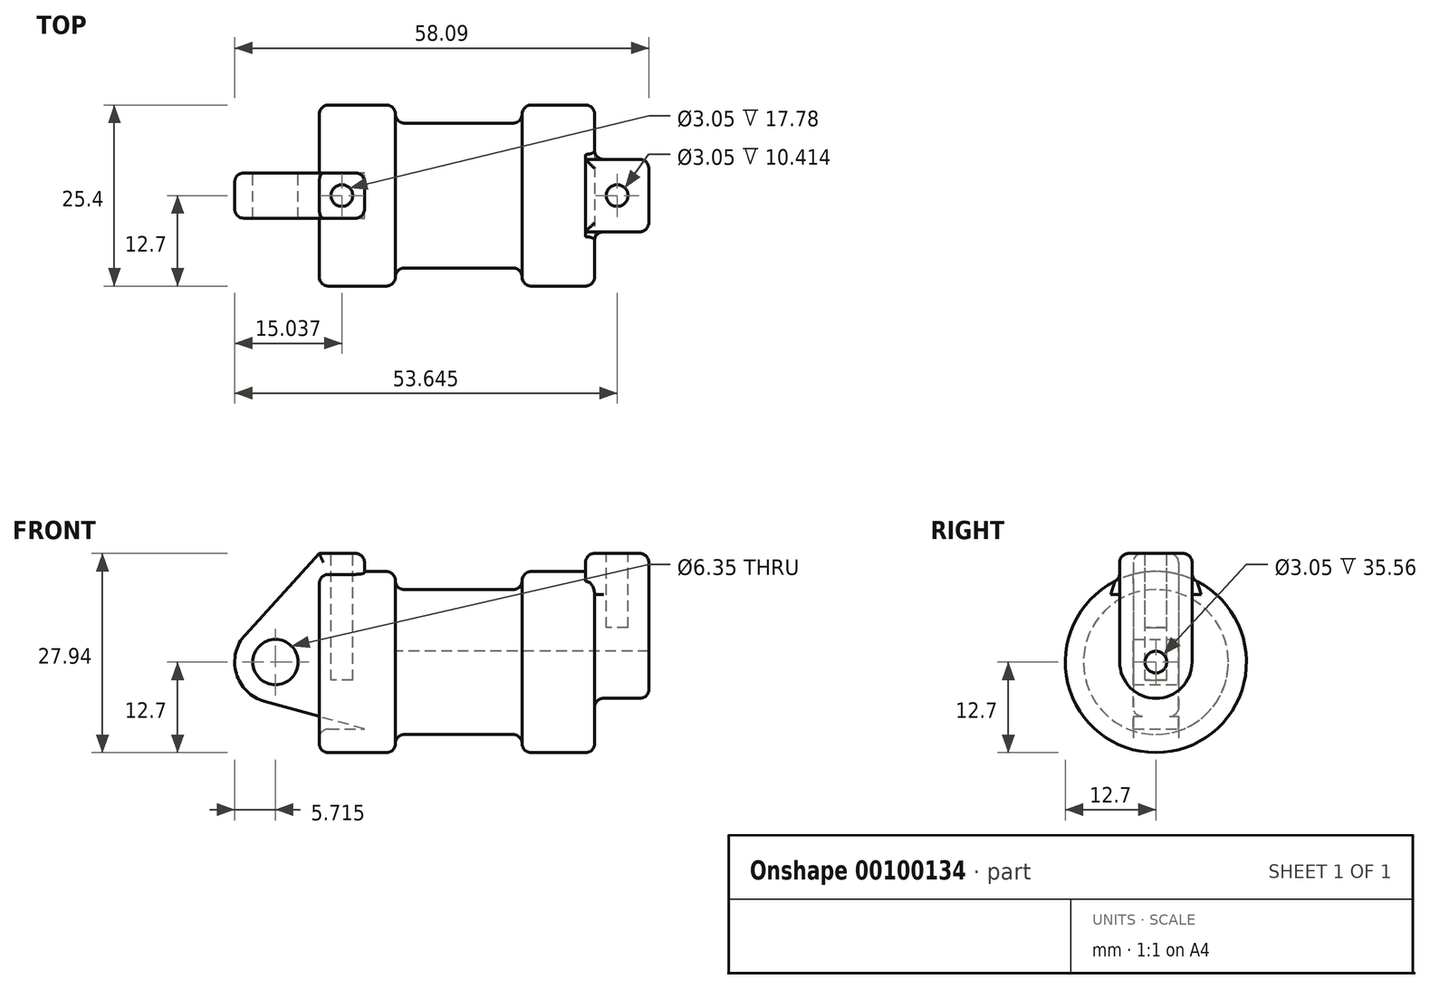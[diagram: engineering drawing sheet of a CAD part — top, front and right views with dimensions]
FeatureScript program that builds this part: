
annotation { "Feature Type Name" : "Feature", "Feature Type Description" : "" }
export const myFeature = defineFeature(function(context is Context, id is Id, definition is map)
    precondition{}
    {
        {
            var Q0;
            Q0=qCreatedBy(makeId("Front.planeOp"),FACE);
            var sketch = newSketch(context, id + "F0", { "sketchPlane" : qUnion([Q0])});
            skLineSegment(sketch, "E0", {"start": v(0, 0) * mm, "end": v(0, 12.7) * mm});
            skLineSegment(sketch, "E1", {"start": v(0, 12.7) * mm, "end": v(10.16, 12.7) * mm});
            skLineSegment(sketch, "E2", {"start": v(10.16, 12.7) * mm, "end": v(10.16, 10.16) * mm});
            skLineSegment(sketch, "E3", {"start": v(10.16, 10.16) * mm, "end": v(27.94, 10.16) * mm});
            skLineSegment(sketch, "E4", {"start": v(27.94, 10.16) * mm, "end": v(27.94, 12.7) * mm});
            skLineSegment(sketch, "E5", {"start": v(27.94, 12.7) * mm, "end": v(38.1, 12.7) * mm});
            skLineSegment(sketch, "E6", {"start": v(38.1, 12.7) * mm, "end": v(38.1, 0) * mm});
            skLineSegment(sketch, "E7", {"start": v(38.1, 0) * mm, "end": v(0, 0) * mm});
            skLineSegment(sketch, "E8", {"start": v(5.84, 15.24) * mm, "end": v(-0.5, 15.24) * mm});
            skLineSegment(sketch, "E9", {"start": v(-0.5, 15.24) * mm, "end": v(-10.88, 3.85) * mm});
            skLineSegment(sketch, "E10", {"start": v(0, 0) * mm, "end": v(-6.65, 0) * mm});
            skCircle(sketch, "E11", {"center": v(-6.65, 0) * mm, "radius": 5.72 * mm});
            skCircle(sketch, "E12", {"center": v(-6.65, 0) * mm, "radius": 3.18 * mm});
            skLineSegment(sketch, "E13", {"start": v(5.84, 15.24) * mm, "end": v(5.84, -9.4) * mm});
            skLineSegment(sketch, "E14", {"start": v(5.84, -9.4) * mm, "end": v(-8.18, -5.5) * mm});
            skSolve(sketch);
        }
        {
            var Q0;
            {var subQ0=sQuery(id+"F0.wireOp",EDGE,"E2");Q0=makeQuery(id+"F0.imprint","IMPRINT",FACE,{"disambiguationData":[TD([[makeQuery(id+"F0.imprint","IMPRINT",EDGE,{"derivedFrom":subQ0}),-1.0]])]});}
            var Q1;
            Q1=sQuery(id+"F0.wireOp",EDGE,"E7");
            revolve(context, id + "F1", {"entities" : qUnion([Q0]), "axis" : qUnion([Q1]), "revolveType" : RevolveType.FULL});
        }
        {
            var Q0;
            {var subQ3=sQuery(id+"F0.wireOp",EDGE,"E0");Q0=makeQuery(id+"F0.imprint","IMPRINT",FACE,{"disambiguationData":[TD([[makeQuery(id+"F0.imprint","IMPRINT",EDGE,{"derivedFrom":subQ3}),1.0]])]});}
            var Q1;
            {var subQ0=sQuery(id+"F0.wireOp",EDGE,"E0");Q1=makeQuery(id+"F0.imprint","IMPRINT",FACE,{"disambiguationData":[TD([[makeQuery(id+"F0.imprint","IMPRINT",EDGE,{"derivedFrom":subQ0}),-1.0]])]});}
            var Q2;
            {var subQ0=sQuery(id+"F0.wireOp",EDGE,"E14");Q2=makeQuery(id+"F0.imprint","IMPRINT",FACE,{"disambiguationData":[TD([[makeQuery(id+"F0.imprint","IMPRINT",EDGE,{"derivedFrom":subQ0}),-1.0]])]});}
            var Q3;
            {var subQ4=sQuery(id+"F0.wireOp",EDGE,"E12");Q3=makeQuery(id+"F0.imprint","IMPRINT",FACE,{"disambiguationData":[TD([[makeQuery(id+"F0.imprint","IMPRINT",EDGE,{"derivedFrom":subQ4}),-1.0]])]});}
            extrude(context, id + "F2", {"entities" : qUnion([Q0, Q1, Q2, Q3]), "operationType" : NewBodyOperationType.ADD, "endBound" : BoundingType.SYMMETRIC, "depth" : 6.35 * mm, "hasSecondDirection" : true, "secondDirectionOppositeDirection" : true, "secondDirectionDepth" : 3.17 * mm});
        }
        {
            var Q0;
            Q0=makeQuery(id+"F1.opRevolve","SWEPT_FACE",FACE,{"disambiguationData":[OSD([sQuery(id+"F0.wireOp",EDGE,"E13")])]});
            extrude(context, id + "F3", {"entities" : qUnion([Q0]), "operationType" : NewBodyOperationType.ADD, "depth" : 6.35 * mm});
        }
        {
            var Q0;
            Q0=makeQuery(id+"F1.opRevolve","SWEPT_FACE",FACE,{"disambiguationData":[OSD([sQuery(id+"F0.wireOp",EDGE,"E6")])]});
            var sketch = newSketch(context, id + "F4", { "sketchPlane" : qUnion([Q0])});
            skCircle(sketch, "E15", {"center": v(0, 0) * mm, "radius": 1.52 * mm});
            skCircle(sketch, "E16", {"center": v(0, 0) * mm, "radius": 5.08 * mm});
            skLineSegment(sketch, "E17", {"start": v(-5.08, 15.24) * mm, "end": v(5.08, 15.24) * mm});
            skLineSegment(sketch, "E18", {"start": v(5.08, 15.24) * mm, "end": v(5.08, 0) * mm});
            skLineSegment(sketch, "E19", {"start": v(-5.08, 15.24) * mm, "end": v(-5.08, 0) * mm});
            skSolve(sketch);
        }
        {
            var Q0;
            {var subQ0=sQuery(id+"F4.wireOp",EDGE,"E18");var subQ1=sQuery(id+"F4.wireOp",EDGE,"E16");var subQ2=makeQuery(id+"F4.imprint","INTERSECT",VERTEX,{"derivedFrom":[subQ1,subQ0]});Q0=makeQuery(id+"F4.imprint","IMPRINT",FACE,{"disambiguationData":[TD([[makeQuery(id+"F4.imprint","IMPRINT",EDGE,{"disambiguationData":[TD([[subQ2,-1.0]])],"derivedFrom":subQ1}),-1.0]])]});}
            var Q1;
            {var subQ0=sQuery(id+"F4.wireOp",EDGE,"E17");Q1=makeQuery(id+"F4.imprint","IMPRINT",FACE,{"disambiguationData":[TD([[makeQuery(id+"F4.imprint","IMPRINT",EDGE,{"derivedFrom":subQ0}),-1.0]])]});}
            var Q2;
            Q2=makeQuery(id+"F4.imprint","IMPRINT",FACE,{"disambiguationData":[TD([[makeQuery(id+"F4.imprint","IMPRINT",EDGE,{"derivedFrom":sQuery(id+"F4.wireOp",EDGE,"E15")}),-1.0]])]});
            extrude(context, id + "F5", {"entities" : qUnion([Q0, Q1, Q2]), "operationType" : NewBodyOperationType.ADD, "depth" : 7.62 * mm, "hasSecondDirection" : true, "secondDirectionOppositeDirection" : true, "secondDirectionDepth" : 1.27 * mm});
        }
        {
            var Q0;
            Q0=makeQuery(id+"F5.boolean.opBoolean","SPLIT",FACE,{"disambiguationData":[TD([makeQuery(id+"F5.opExtrude","SWEPT_FACE",FACE,{"disambiguationData":[OSD([sQuery(id+"F4.wireOp",EDGE,"E15")])]})])],"derivedFrom":makeQuery(id+"F1.opRevolve","SWEPT_FACE",FACE,{"disambiguationData":[OSD([sQuery(id+"F0.wireOp",EDGE,"E6")])]})});
            var Q1;
            Q1=makeQuery(id+"F1.opRevolve","SWEPT_FACE",FACE,{"disambiguationData":[OSD([sQuery(id+"F0.wireOp",EDGE,"E2")])]});
            var Q2;
            Q2=makeQuery(id+"F1.opRevolve","SWEPT_BODY",BODY,{"disambiguationData":[OSD([sQuery(id+"F0.wireOp",EDGE,"E1"),sQuery(id+"F0.wireOp",EDGE,"E2"),sQuery(id+"F0.wireOp",EDGE,"E3"),sQuery(id+"F0.wireOp",EDGE,"E4"),sQuery(id+"F0.wireOp",EDGE,"E5"),sQuery(id+"F0.wireOp",EDGE,"E6"),sQuery(id+"F0.wireOp",EDGE,"E7"),sQuery(id+"F0.wireOp",EDGE,"E13")])]});
            extrude(context, id + "F6", {"entities" : qUnion([Q0]), "operationType" : NewBodyOperationType.ADD, "endBound" : BoundingType.UP_TO_SURFACE, "oppositeDirection" : true, "endBoundEntityFace" : qUnion([Q1]), "endBoundEntityBody" : qUnion([Q2]), "depth" : 25.4 * mm});
        }
        {
            var Q0;
            Q0=makeQuery(id+"F5.boolean.opBoolean","SPLIT",FACE,{"disambiguationData":[TD([makeQuery(id+"F5.opExtrude","SWEPT_FACE",FACE,{"disambiguationData":[OSD([sQuery(id+"F4.wireOp",EDGE,"E15")])]})])],"derivedFrom":makeQuery(id+"F1.opRevolve","SWEPT_FACE",FACE,{"disambiguationData":[OSD([sQuery(id+"F0.wireOp",EDGE,"E6")])]})});
            var Q1;
            Q1=makeQuery(id+"F1.opRevolve","SWEPT_FACE",FACE,{"disambiguationData":[OSD([sQuery(id+"F0.wireOp",EDGE,"E2")])]});
            extrude(context, id + "F7", {"entities" : qUnion([Q0]), "operationType" : NewBodyOperationType.REMOVE, "endBound" : BoundingType.UP_TO_SURFACE, "oppositeDirection" : true, "endBoundEntityFace" : qUnion([Q1]), "depth" : 25.4 * mm});
        }
        {
            var Q0;
            Q0=makeQuery(id+"F2.opExtrude","SWEPT_FACE",FACE,{"disambiguationData":[OSD([sQuery(id+"F0.wireOp",EDGE,"E8")])]});
            var sketch = newSketch(context, id + "F8", { "sketchPlane" : qUnion([Q0])});
            skCircle(sketch, "E20", {"center": v(2.67, 0) * mm, "radius": 1.52 * mm});
            skSolve(sketch);
        }
        {
            var Q0;
            Q0=makeQuery(id+"F8.imprint","IMPRINT",FACE,{"disambiguationData":[TD([[makeQuery(id+"F8.imprint","IMPRINT",EDGE,{"derivedFrom":sQuery(id+"F8.wireOp",EDGE,"E20")}),1.0]])]});
            extrude(context, id + "F9", {"entities" : qUnion([Q0]), "operationType" : NewBodyOperationType.REMOVE, "oppositeDirection" : true, "depth" : 17.78 * mm});
        }
        {
            var Q0;
            Q0=makeQuery(id+"F5.opExtrude","SWEPT_FACE",FACE,{"disambiguationData":[OSD([sQuery(id+"F4.wireOp",EDGE,"E17")])]});
            var sketch = newSketch(context, id + "F10", { "sketchPlane" : qUnion([Q0])});
            skLineSegment(sketch, "E21", {"start": v(36.83, 0) * mm, "end": v(45.72, 0) * mm, "construction": true});
            skCircle(sketch, "E22", {"center": v(41.28, 0) * mm, "radius": 1.52 * mm});
            skSolve(sketch);
        }
        {
            var Q0;
            Q0=makeQuery(id+"F10.imprint","IMPRINT",FACE,{"disambiguationData":[TD([[makeQuery(id+"F10.imprint","IMPRINT",EDGE,{"derivedFrom":sQuery(id+"F10.wireOp",EDGE,"E22")}),1.0]])]});
            extrude(context, id + "F11", {"entities" : qUnion([Q0]), "operationType" : NewBodyOperationType.REMOVE, "oppositeDirection" : true, "depth" : 10.4 * mm});
        }
        {
            var Q0;
            Q0=makeQuery(id+"F2.opExtrude","CAP_EDGE",EDGE,{"disambiguationData":[OSD([sQuery(id+"F0.wireOp",EDGE,"E8")])],"isStart":false});
            var Q1;
            Q1=makeQuery(id+"F2.opExtrude","SWEPT_EDGE",EDGE,{"disambiguationData":[OSD([sQuery(id+"F0.wireOp",EDGE,"E8"),sQuery(id+"F0.wireOp",EDGE,"E13")])]});
            var Q2;
            Q2=makeQuery(id+"F2.opExtrude","CAP_EDGE",EDGE,{"disambiguationData":[OSD([sQuery(id+"F0.wireOp",EDGE,"E8")])],"isStart":true});
            var Q3;
            {var subQ0=sQuery(id+"F0.wireOp",EDGE,"E1");var subQ1=sQuery(id+"F0.wireOp",EDGE,"E13");Q3=makeQuery(id+"F2.boolean.opBoolean","SPLIT",EDGE,{"disambiguationData":[topologyDisambiguationEdgeConnected([makeQuery(id+"F2.opExtrude","SWEPT_FACE",FACE,{"disambiguationData":[OSD([subQ1])]})])],"derivedFrom":makeQuery(id+"F1.opRevolve","SWEPT_EDGE",EDGE,{"disambiguationData":[OSD([subQ0,subQ1])]})});}
            var Q4;
            {var subQ0=sQuery(id+"F0.wireOp",EDGE,"E13");var subQ1=sQuery(id+"F0.wireOp",EDGE,"E14");var subQ2=sQuery(id+"F0.wireOp",EDGE,"E12");var subQ3=sQuery(id+"F0.wireOp",EDGE,"E11");var subQ4=sQuery(id+"F0.wireOp",EDGE,"E9");var subQ5=sQuery(id+"F0.wireOp",EDGE,"E8");var subQ6=sQuery(id+"F0.wireOp",EDGE,"E1");Q4=makeQuery(id+"F3.opExtrude","SWEPT_EDGE",EDGE,{"disambiguationData":[OSD([subQ6,subQ5,subQ4,subQ3,subQ2,subQ0,subQ1]),TDD([makeQuery(id+"F2.boolean.opBoolean","TWEAK_VERTEX",VERTEX,{"derivedFrom":[makeQuery(id+"F1.opRevolve","SWEPT_FACE",FACE,{"disambiguationData":[OSD([subQ6])]}),makeQuery(id+"F1.opRevolve","SWEPT_FACE",FACE,{"disambiguationData":[OSD([subQ0])]}),makeQuery(id+"F2.opExtrude","CAP_FACE",FACE,{"disambiguationData":[OSD([subQ5,subQ4,subQ3,subQ2,subQ0,subQ1])],"isStart":false}),makeQuery(id+"F2.opExtrude","SWEPT_FACE",FACE,{"disambiguationData":[OSD([subQ0])]})]})])]});}
            var Q5;
            {var subQ0=sQuery(id+"F0.wireOp",EDGE,"E13");var subQ1=sQuery(id+"F0.wireOp",EDGE,"E14");var subQ2=sQuery(id+"F0.wireOp",EDGE,"E12");var subQ3=sQuery(id+"F0.wireOp",EDGE,"E11");var subQ4=sQuery(id+"F0.wireOp",EDGE,"E9");var subQ5=sQuery(id+"F0.wireOp",EDGE,"E8");var subQ6=sQuery(id+"F0.wireOp",EDGE,"E1");Q5=makeQuery(id+"F3.opExtrude","SWEPT_EDGE",EDGE,{"disambiguationData":[OSD([subQ6,subQ5,subQ4,subQ3,subQ2,subQ0,subQ1]),TDD([makeQuery(id+"F2.boolean.opBoolean","TWEAK_VERTEX",VERTEX,{"derivedFrom":[makeQuery(id+"F1.opRevolve","SWEPT_FACE",FACE,{"disambiguationData":[OSD([subQ6])]}),makeQuery(id+"F1.opRevolve","SWEPT_FACE",FACE,{"disambiguationData":[OSD([subQ0])]}),makeQuery(id+"F2.opExtrude","CAP_FACE",FACE,{"disambiguationData":[OSD([subQ5,subQ4,subQ3,subQ2,subQ0,subQ1])],"isStart":true}),makeQuery(id+"F2.opExtrude","SWEPT_FACE",FACE,{"disambiguationData":[OSD([subQ0])]})]})])]});}
            var Q6;
            {var subQ0=sQuery(id+"F0.wireOp",EDGE,"E13");Q6=makeQuery(id+"F2.boolean.opBoolean","SPLIT",EDGE,{"disambiguationData":[topologyDisambiguationEdgeConnected([makeQuery(id+"F2.opExtrude","SWEPT_FACE",FACE,{"disambiguationData":[OSD([subQ0])]})])],"derivedFrom":makeQuery(id+"F2.opExtrude","CAP_EDGE",EDGE,{"disambiguationData":[OSD([subQ0])],"isStart":true})});}
            var Q7;
            {var subQ0=sQuery(id+"F0.wireOp",EDGE,"E13");Q7=makeQuery(id+"F2.boolean.opBoolean","SPLIT",EDGE,{"disambiguationData":[topologyDisambiguationEdgeConnected([makeQuery(id+"F2.opExtrude","SWEPT_FACE",FACE,{"disambiguationData":[OSD([subQ0])]})])],"derivedFrom":makeQuery(id+"F2.opExtrude","CAP_EDGE",EDGE,{"disambiguationData":[OSD([subQ0])],"isStart":false})});}
            var Q8;
            Q8=makeQuery(id+"F2.opExtrude","CAP_EDGE",EDGE,{"disambiguationData":[OSD([sQuery(id+"F0.wireOp",EDGE,"E9")])],"isStart":true});
            var Q9;
            Q9=makeQuery(id+"F2.opExtrude","CAP_EDGE",EDGE,{"disambiguationData":[OSD([sQuery(id+"F0.wireOp",EDGE,"E9")])],"isStart":false});
            var Q10;
            Q10=makeQuery(id+"F1.opRevolve","SWEPT_EDGE",EDGE,{"disambiguationData":[OSD([sQuery(id+"F0.wireOp",EDGE,"E1"),sQuery(id+"F0.wireOp",EDGE,"E2")])]});
            var Q11;
            Q11=makeQuery(id+"F1.opRevolve","SWEPT_EDGE",EDGE,{"disambiguationData":[OSD([sQuery(id+"F0.wireOp",EDGE,"E2"),sQuery(id+"F0.wireOp",EDGE,"E3")])]});
            var Q12;
            Q12=makeQuery(id+"F1.opRevolve","SWEPT_EDGE",EDGE,{"disambiguationData":[OSD([sQuery(id+"F0.wireOp",EDGE,"E4"),sQuery(id+"F0.wireOp",EDGE,"E5")])]});
            var Q13;
            Q13=makeQuery(id+"F1.opRevolve","SWEPT_EDGE",EDGE,{"disambiguationData":[OSD([sQuery(id+"F0.wireOp",EDGE,"E3"),sQuery(id+"F0.wireOp",EDGE,"E4")])]});
            var Q14;
            Q14=makeQuery(id+"F1.opRevolve","SWEPT_EDGE",EDGE,{"disambiguationData":[OSD([sQuery(id+"F0.wireOp",EDGE,"E5"),sQuery(id+"F0.wireOp",EDGE,"E6")])]});
            var Q15;
            Q15=makeQuery(id+"F5.opExtrude","SWEPT_EDGE",EDGE,{"disambiguationData":[OSD([sQuery(id+"F4.wireOp",EDGE,"E17"),sQuery(id+"F4.wireOp",EDGE,"E19")])]});
            var Q16;
            Q16=makeQuery(id+"F5.opExtrude","CAP_EDGE",EDGE,{"disambiguationData":[OSD([sQuery(id+"F4.wireOp",EDGE,"E17")])],"isStart":true});
            var Q17;
            Q17=makeQuery(id+"F5.opExtrude","SWEPT_EDGE",EDGE,{"disambiguationData":[OSD([sQuery(id+"F4.wireOp",EDGE,"E17"),sQuery(id+"F4.wireOp",EDGE,"E18")])]});
            var Q18;
            Q18=makeQuery(id+"F5.opExtrude","CAP_EDGE",EDGE,{"disambiguationData":[OSD([sQuery(id+"F4.wireOp",EDGE,"E17")])],"isStart":false});
            var Q19;
            Q19=makeQuery(id+"F5.opExtrude","CAP_EDGE",EDGE,{"disambiguationData":[OSD([sQuery(id+"F4.wireOp",EDGE,"E19")])],"isStart":false});
            var Q20;
            Q20=makeQuery(id+"F5.boolean.opBoolean","INTERSECT",EDGE,{"derivedFrom":[makeQuery(id+"F1.opRevolve","SWEPT_FACE",FACE,{"disambiguationData":[OSD([sQuery(id+"F0.wireOp",EDGE,"E6")])]}),makeQuery(id+"F5.opExtrude","SWEPT_FACE",FACE,{"disambiguationData":[OSD([sQuery(id+"F4.wireOp",EDGE,"E19")])]})]});
            var Q21;
            Q21=makeQuery(id+"F5.boolean.opBoolean","INTERSECT",EDGE,{"derivedFrom":[makeQuery(id+"F1.opRevolve","SWEPT_FACE",FACE,{"disambiguationData":[OSD([sQuery(id+"F0.wireOp",EDGE,"E6")])]}),makeQuery(id+"F5.opExtrude","SWEPT_FACE",FACE,{"disambiguationData":[OSD([sQuery(id+"F4.wireOp",EDGE,"E16")])]})]});
            fillet(context, id + "F12", {"entities" : qUnion([Q0, Q1, Q2, Q3, Q4, Q5, Q6, Q7, Q8, Q9, Q10, Q11, Q12, Q13, Q14, Q15, Q16, Q17, Q18, Q19, Q20, Q21]), "radius" : 1.27 * mm, "tangentPropagation" : true, "allowEdgeOverflow" : false});
        }
        {
            var Q0;
            Q0=makeQuery(id+"F3.opExtrude","CAP_EDGE",EDGE,{"disambiguationData":[OSD([sQuery(id+"F0.wireOp",EDGE,"E1"),sQuery(id+"F0.wireOp",EDGE,"E13")])],"isStart":false});
            var Q1;
            {var subQ0=sQuery(id+"F0.wireOp",EDGE,"E13");var subQ1=makeQuery(id+"F2.opExtrude","CAP_FACE",FACE,{"disambiguationData":[OSD([sQuery(id+"F0.wireOp",EDGE,"E8"),sQuery(id+"F0.wireOp",EDGE,"E9"),sQuery(id+"F0.wireOp",EDGE,"E11"),sQuery(id+"F0.wireOp",EDGE,"E12"),subQ0,sQuery(id+"F0.wireOp",EDGE,"E14")])],"isStart":false});Q1=makeQuery(id+"F3.boolean.opBoolean","SPLIT",EDGE,{"disambiguationData":[topologyDisambiguationEdgeConnected([subQ1])],"derivedFrom":makeQuery(id+"F3.opExtrude","CAP_EDGE",EDGE,{"disambiguationData":[OSD([subQ0]),TDD([makeQuery(id+"F2.boolean.opBoolean","SPLIT",EDGE,{"disambiguationData":[topologyDisambiguationEdgeConnected([makeQuery(id+"F1.opRevolve","SWEPT_FACE",FACE,{"disambiguationData":[OSD([subQ0])]})])],"derivedFrom":makeQuery(id+"F2.opExtrude","CAP_EDGE",EDGE,{"disambiguationData":[OSD([subQ0])],"isStart":false})})])],"isStart":false})});}
            fillet(context, id + "F13", {"entities" : qUnion([Q0, Q1]), "radius" : 1.27 * mm, "tangentPropagation" : true, "allowEdgeOverflow" : false});
        }
    });
